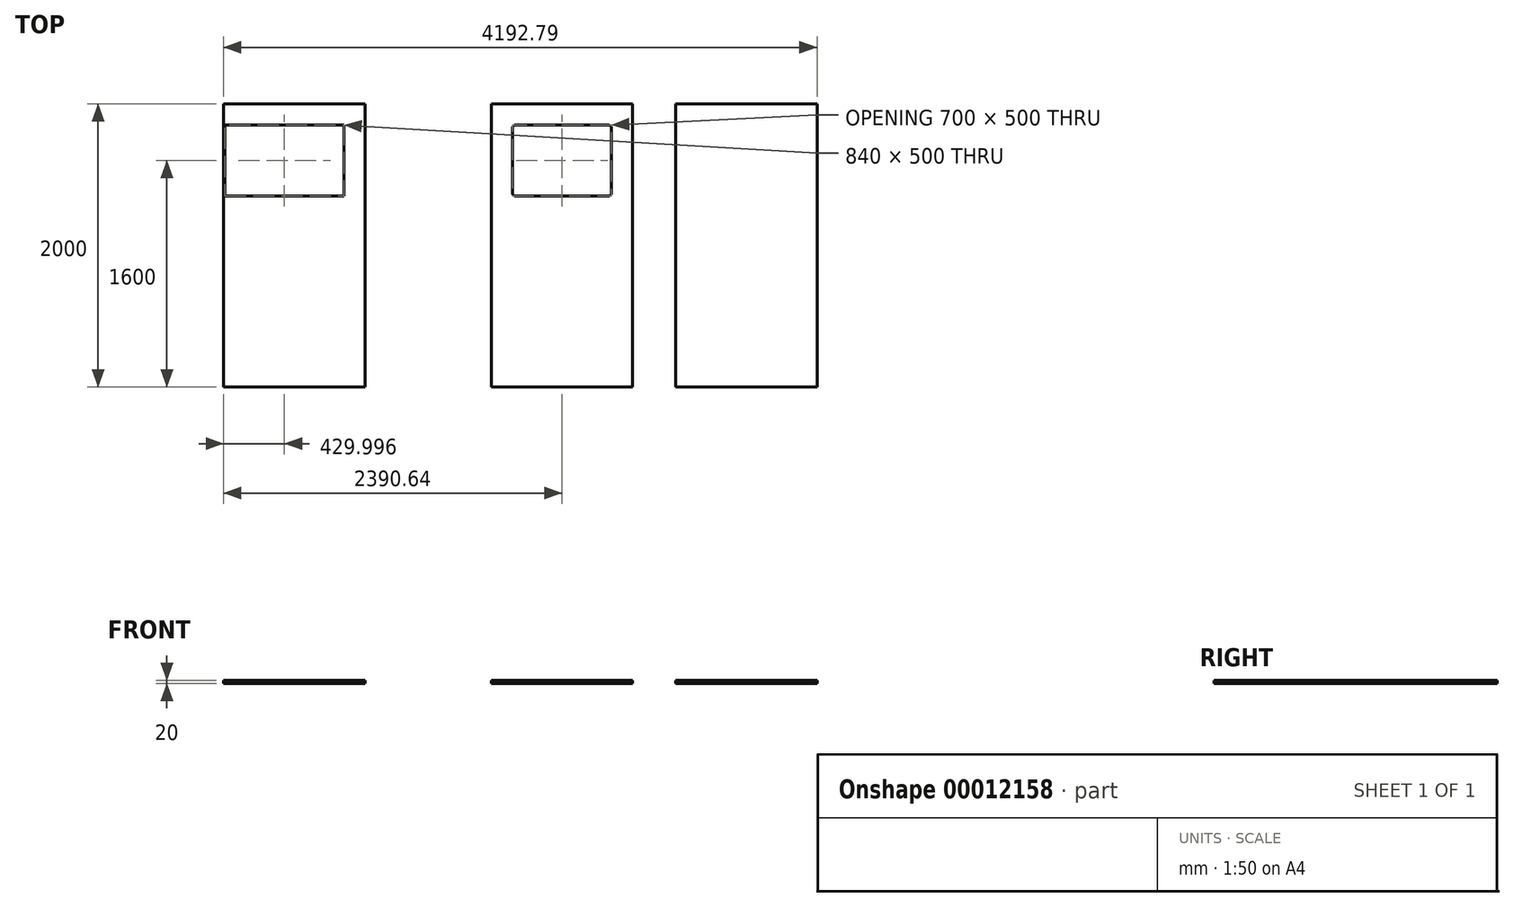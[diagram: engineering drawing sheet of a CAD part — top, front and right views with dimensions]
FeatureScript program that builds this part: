
annotation { "Feature Type Name" : "Feature", "Feature Type Description" : "" }
export const myFeature = defineFeature(function(context is Context, id is Id, definition is map)
    precondition{}
    {
        {
            var Q0;
            Q0=qCreatedBy(makeId("Top.planeOp"),FACE);
            var sketch = newSketch(context, id + "F0", { "sketchPlane" : qUnion([Q0])});
            skLineSegment(sketch, "E0.rect.bottom", {"start": v(500, 1000) * mm, "end": v(-500, 1000) * mm});
            skLineSegment(sketch, "E0.rect.top", {"start": v(500, -1000) * mm, "end": v(-500, -1000) * mm});
            skLineSegment(sketch, "E0.rect.left", {"start": v(500, 1000) * mm, "end": v(500, -1000) * mm});
            skLineSegment(sketch, "E0.rect.right", {"start": v(-500, 1000) * mm, "end": v(-500, -1000) * mm});
            skPoint(sketch, "E0.rect.middle", {"position": v(0, 0) * mm});
            skSolve(sketch);
        }
        {
            var Q0;
            Q0=makeQuery(id+"F0.imprint","IMPRINT",FACE,{"disambiguationData":[TD([[makeQuery(id+"F0.imprint","IMPRINT",EDGE,{"derivedFrom":sQuery(id+"F0.wireOp",EDGE,"E0.rect.bottom")}),1.0]])]});
            extrude(context, id + "F1", {"entities" : qUnion([Q0]), "depth" : 20 * mm});
        }
        {
            var Q0;
            Q0=qCreatedBy(makeId("Top.planeOp"),FACE);
            var sketch = newSketch(context, id + "F2", { "sketchPlane" : qUnion([Q0])});
            skLineSegment(sketch, "E1.rect.bottom", {"start": v(-802.15, -1000) * mm, "end": v(-1802.15, -1000) * mm});
            skLineSegment(sketch, "E1.rect.top", {"start": v(-802.15, 1000) * mm, "end": v(-1802.15, 1000) * mm});
            skLineSegment(sketch, "E1.rect.left", {"start": v(-802.15, -1000) * mm, "end": v(-802.15, 1000) * mm});
            skLineSegment(sketch, "E1.rect.right", {"start": v(-1802.15, -1000) * mm, "end": v(-1802.15, 1000) * mm});
            skPoint(sketch, "E1.rect.middle", {"position": v(-1302.15, 0) * mm});
            skSolve(sketch);
        }
        {
            var Q0;
            Q0=makeQuery(id+"F2.imprint","IMPRINT",FACE,{"disambiguationData":[TD([[makeQuery(id+"F2.imprint","IMPRINT",EDGE,{"derivedFrom":sQuery(id+"F2.wireOp",EDGE,"E1.rect.bottom")}),-1.0]])]});
            extrude(context, id + "F3", {"entities" : qUnion([Q0]), "depth" : 20 * mm});
        }
        {
            var Q0;
            Q0=makeQuery(id+"F3.opExtrude","CAP_FACE",FACE,{"disambiguationData":[OSD([sQuery(id+"F2.wireOp",EDGE,"E1.rect.bottom"),sQuery(id+"F2.wireOp",EDGE,"E1.rect.top"),sQuery(id+"F2.wireOp",EDGE,"E1.rect.left"),sQuery(id+"F2.wireOp",EDGE,"E1.rect.right")])],"isStart":false});
            var sketch = newSketch(context, id + "F4", { "sketchPlane" : qUnion([Q0])});
            skLineSegment(sketch, "E2.rect.bottom", {"start": v(-952.15, 850) * mm, "end": v(-1652.15, 850) * mm});
            skLineSegment(sketch, "E2.rect.top", {"start": v(-952.15, 350) * mm, "end": v(-1652.15, 350) * mm});
            skLineSegment(sketch, "E2.rect.left", {"start": v(-952.15, 850) * mm, "end": v(-952.15, 350) * mm});
            skLineSegment(sketch, "E2.rect.right", {"start": v(-1652.15, 850) * mm, "end": v(-1652.15, 350) * mm});
            skPoint(sketch, "E2.rect.middle", {"position": v(-1302.15, 600) * mm});
            skLineSegment(sketch, "E3", {"start": v(-1302.15, 1000) * mm, "end": v(-1302.15, -1000) * mm, "construction": true});
            skSolve(sketch);
        }
        {
            var Q0;
            Q0=makeQuery(id+"F4.imprint","IMPRINT",FACE,{"disambiguationData":[TD([[makeQuery(id+"F4.imprint","IMPRINT",EDGE,{"derivedFrom":sQuery(id+"F4.wireOp",EDGE,"E2.rect.bottom")}),1.0]])]});
            extrude(context, id + "F5", {"entities" : qUnion([Q0]), "operationType" : NewBodyOperationType.REMOVE, "endBound" : BoundingType.THROUGH_ALL, "oppositeDirection" : true, "depth" : 25 * mm});
        }
        {
            var Q0;
            Q0=makeQuery(id+"F5.boolean.opBoolean","COPY",EDGE,{"derivedFrom":makeQuery(id+"F5.opExtrude","SWEPT_EDGE",EDGE,{"disambiguationData":[OSD([sQuery(id+"F4.wireOp",EDGE,"E2.rect.bottom"),sQuery(id+"F4.wireOp",EDGE,"E2.rect.right")])]})});
            var Q1;
            Q1=makeQuery(id+"F5.boolean.opBoolean","COPY",EDGE,{"derivedFrom":makeQuery(id+"F5.opExtrude","SWEPT_EDGE",EDGE,{"disambiguationData":[OSD([sQuery(id+"F4.wireOp",EDGE,"E2.rect.bottom"),sQuery(id+"F4.wireOp",EDGE,"E2.rect.left")])]})});
            var Q2;
            Q2=makeQuery(id+"F5.boolean.opBoolean","COPY",EDGE,{"derivedFrom":makeQuery(id+"F5.opExtrude","SWEPT_EDGE",EDGE,{"disambiguationData":[OSD([sQuery(id+"F4.wireOp",EDGE,"E2.rect.top"),sQuery(id+"F4.wireOp",EDGE,"E2.rect.left")])]})});
            var Q3;
            Q3=makeQuery(id+"F5.boolean.opBoolean","COPY",EDGE,{"derivedFrom":makeQuery(id+"F5.opExtrude","SWEPT_EDGE",EDGE,{"disambiguationData":[OSD([sQuery(id+"F4.wireOp",EDGE,"E2.rect.top"),sQuery(id+"F4.wireOp",EDGE,"E2.rect.right")])]})});
            fillet(context, id + "F6", {"entities" : qUnion([Q0, Q1, Q2, Q3]), "radius" : 20 * mm, "tangentPropagation" : true, "allowEdgeOverflow" : false});
        }
        {
            var Q0;
            Q0=qCreatedBy(makeId("Top.planeOp"),FACE);
            var sketch = newSketch(context, id + "F7", { "sketchPlane" : qUnion([Q0])});
            skLineSegment(sketch, "E4.rect.bottom", {"start": v(-2692.8, 1000) * mm, "end": v(-3692.8, 1000) * mm});
            skLineSegment(sketch, "E4.rect.top", {"start": v(-2692.8, -1000) * mm, "end": v(-3692.8, -1000) * mm});
            skLineSegment(sketch, "E4.rect.left", {"start": v(-2692.8, 1000) * mm, "end": v(-2692.8, -1000) * mm});
            skLineSegment(sketch, "E4.rect.right", {"start": v(-3692.8, 1000) * mm, "end": v(-3692.8, -1000) * mm});
            skPoint(sketch, "E4.rect.middle", {"position": v(-3192.8, 0) * mm});
            skSolve(sketch);
        }
        {
            var Q0;
            Q0=makeQuery(id+"F7.imprint","IMPRINT",FACE,{"disambiguationData":[TD([[makeQuery(id+"F7.imprint","IMPRINT",EDGE,{"derivedFrom":sQuery(id+"F7.wireOp",EDGE,"E4.rect.bottom")}),1.0]])]});
            extrude(context, id + "F8", {"entities" : qUnion([Q0]), "depth" : 20 * mm});
        }
        {
            var Q0;
            Q0=makeQuery(id+"F8.opExtrude","CAP_FACE",FACE,{"disambiguationData":[OSD([sQuery(id+"F7.wireOp",EDGE,"E4.rect.bottom"),sQuery(id+"F7.wireOp",EDGE,"E4.rect.top"),sQuery(id+"F7.wireOp",EDGE,"E4.rect.left"),sQuery(id+"F7.wireOp",EDGE,"E4.rect.right")])],"isStart":false});
            var sketch = newSketch(context, id + "F9", { "sketchPlane" : qUnion([Q0])});
            skLineSegment(sketch, "E5.rect.bottom", {"start": v(-2842.8, 350) * mm, "end": v(-3682.8, 350) * mm});
            skLineSegment(sketch, "E5.rect.top", {"start": v(-2842.8, 850) * mm, "end": v(-3682.8, 850) * mm});
            skLineSegment(sketch, "E5.rect.left", {"start": v(-2842.8, 350) * mm, "end": v(-2842.8, 850) * mm});
            skLineSegment(sketch, "E5.rect.right", {"start": v(-3682.8, 350) * mm, "end": v(-3682.8, 850) * mm});
            skPoint(sketch, "E5.rect.middle", {"position": v(-3262.8, 600) * mm});
            skSolve(sketch);
        }
        {
            var Q0;
            Q0=makeQuery(id+"F9.imprint","IMPRINT",FACE,{"disambiguationData":[TD([[makeQuery(id+"F9.imprint","IMPRINT",EDGE,{"derivedFrom":sQuery(id+"F9.wireOp",EDGE,"E5.rect.bottom")}),-1.0]])]});
            extrude(context, id + "F10", {"entities" : qUnion([Q0]), "operationType" : NewBodyOperationType.REMOVE, "endBound" : BoundingType.THROUGH_ALL, "oppositeDirection" : true, "depth" : 25 * mm});
        }
    });
